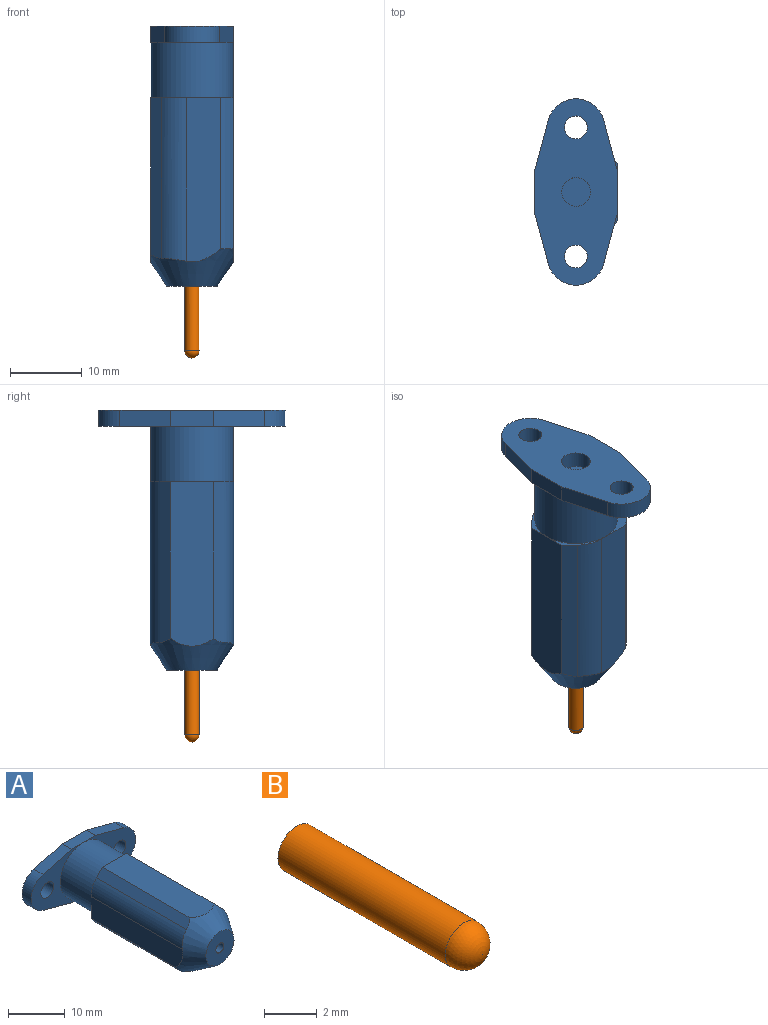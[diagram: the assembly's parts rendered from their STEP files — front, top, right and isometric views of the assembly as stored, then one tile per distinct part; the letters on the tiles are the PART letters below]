
ASSEMBLY  parts=2 mates=1
PART A: 30 faces, bbox 27.6x37.9x15.6 mm
  f0: cylinder r=1mm len=15mm, axis (0,-1,0), area 94.2mm2, adj f26,f29
  f1: cone r=3.5mm half-angle=34deg, axis (0,1,0), area 158.3mm2, adj f18,f19,f20,f21,f22,f23,f24,f25
  f2: cylinder r=5.75mm len=11.5mm, axis (0,1,0), area 278.2mm2, adj f7,f17
  f3: cylinder r=1.6mm len=3.2mm, axis (0,-1,0), area 23.1mm2, adj f6,f7
  f4: cylinder r=1.6mm len=3.2mm, axis (0,-1,0), area 23.1mm2, adj f6,f7
  f5: cylinder r=2mm len=4mm, axis (0,-1,0), area 28.9mm2, adj f6,f16
  f6: plane 26x11.53mm, normal (0,1,0), area 209.9mm2, adj f3,f4,f5,f8,f9,f10,f11,f12
  f7: plane 26x11.53mm, normal (0,-1,0), area 118.6mm2, adj f2,f3,f4,f8,f9,f10,f11,f12
  f8: plane 6x2.3mm, normal (0,0,-1), area 13.8mm2, adj f6,f7,f9,f15
  f9: plane 7.04x2.3mm, normal (-0.26,0,-0.97), area 16.8mm2, adj f6,f7,f8,f10
  f10: cylinder r=4mm len=7.72mm, axis (0,-1,0), area 24mm2, adj f6,f7,f9,f11
  f11: plane 7.04x2.3mm, normal (-0.26,0,0.97), area 16.8mm2, adj f6,f7,f10,f12
  f12: plane 6x2.3mm, normal (0,0,1), area 13.8mm2, adj f6,f7,f11,f13
  f13: plane 7.04x2.3mm, normal (0.26,0,0.97), area 16.8mm2, adj f6,f7,f12,f14
  f14: cylinder r=4mm len=7.72mm, axis (0,-1,0), area 24mm2, adj f6,f7,f13,f15
  f15: plane 7.04x2.3mm, normal (0.26,0,-0.97), area 16.8mm2, adj f6,f7,f8,f14
  f16: plane 4x4mm, normal (0,1,0), area 12.6mm2, adj f5
  f17: plane 11.6x11.53mm, normal (0,1,0), area 17.6mm2, adj f2,f18,f19,f20,f21,f22,f23,f24
  f18: plane 23.58x6.65mm, normal (0,0,1), area 135.4mm2, adj f1,f17,f19,f22
  f19: plane 22.71x1.86mm, normal (0.73,0,0.68), area 47.1mm2, adj f1,f17,f18,f24
  f20: plane 24.47x6.29mm, normal (1,0,0), area 105.8mm2, adj f1,f17,f24,f27
  f21: plane 24.47x6.29mm, normal (-1,0,0), area 105.8mm2, adj f1,f17,f25,f28
  f22: plane 22.71x1.86mm, normal (-0.73,0,0.68), area 47.1mm2, adj f1,f17,f18,f25
  f23: plane 24.02x9.04mm, normal (0,0,-1), area 177.4mm2, adj f1,f17,f27,f28
  f24: cylinder r=5mm len=22.81mm, axis (0,-1,0), area 85mm2, adj f1,f17,f19,f20
  f25: cylinder r=5mm len=22.81mm, axis (0,-1,0), area 85mm2, adj f1,f17,f21,f22
  f26: plane 7x7mm, normal (0,-1,0), area 35.3mm2, adj f0,f1
  f27: cylinder r=7mm len=21.1mm, axis (0,-1,0), area 54.9mm2, adj f1,f17,f20,f23
  f28: cylinder r=7mm len=21.1mm, axis (0,-1,0), area 54.9mm2, adj f1,f17,f21,f23
  f29: plane 2x2mm, normal (0,-1,0), area 3.1mm2, adj f0
PART B: 3 faces, bbox 2x10x2 mm
  f0: cylinder r=1mm len=9mm, axis (0,1,0), area 56.5mm2, adj f1,f2
  f1: plane 2x2mm, normal (0,1,0), area 3.1mm2, adj f0
  f2: sphere r=1mm, area 6.3mm2, adj f0
PLACE A rot(axis=(0.58,-0.58,-0.58),120deg) t=(-48.98,19.56,-3.11)mm
PLACE B rot(axis=(0.58,-0.58,-0.58),120deg) t=(-48.98,19.56,-3.11)mm
MATE slider B.f0 <-> A.f0  axis (0,0,1) through (-48.98,19.56,-37.11)mm
